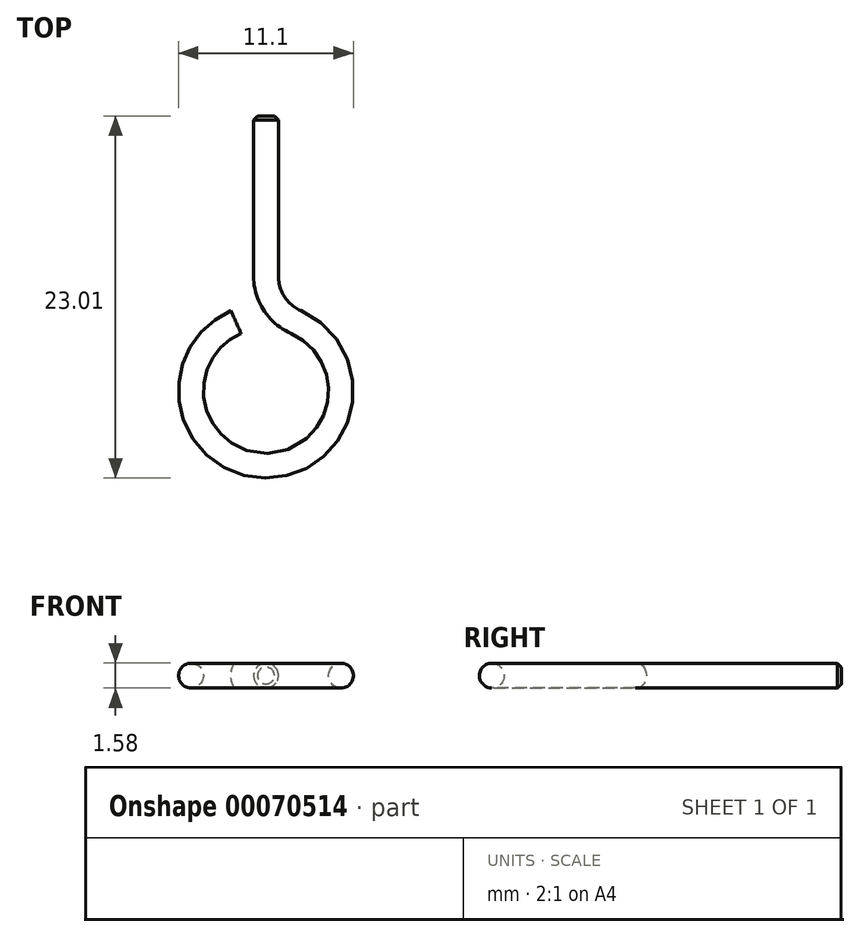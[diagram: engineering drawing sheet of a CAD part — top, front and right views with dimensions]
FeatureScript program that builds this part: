
annotation { "Feature Type Name" : "Feature", "Feature Type Description" : "" }
export const myFeature = defineFeature(function(context is Context, id is Id, definition is map)
    precondition{}
    {
        {
            var Q0;
            Q0=qCreatedBy(makeId("Top.planeOp"),FACE);
            var sketch = newSketch(context, id + "F0", { "sketchPlane" : qUnion([Q0])});
            skLineSegment(sketch, "E0", {"start": v(0, 17.46) * mm, "end": v(0, 7.27) * mm});
            skArc(sketch, "E1", {"start": v(1.9, 4.36) * mm, "mid": v(0, -4.76) * mm, "end": v(-1.9, 4.36) * mm});
            skPoint(sketch, "E2.visualSharp", {"position": v(0, 4.76) * mm});
            skArc(sketch, "E2.filletArc", {"start": v(0, 7.27) * mm, "mid": v(0.52, 5.54) * mm, "end": v(1.9, 4.36) * mm});
            skSolve(sketch);
        }
        {
            var Q0;
            Q0=qCreatedBy(makeId("Front.planeOp"),FACE);
            var Q1;
            Q1=sQuery(id+"F0.wireOp",VERTEX,"E0.start");
            cPlane(context, id + "F1", {"entities" : qUnion([Q0, Q1]), "cplaneType" : CPlaneType.PLANE_POINT, "offset" : 152.4 * mm, "width" : 152.4 * mm, "height" : 152.4 * mm});
        }
        {
            var Q0;
            Q0=qCreatedBy(id+"F1.planeOp",FACE);
            var sketch = newSketch(context, id + "F2", { "sketchPlane" : qUnion([Q0])});
            skCircle(sketch, "E3", {"center": v(0, 0) * mm, "radius": 0.79 * mm});
            skSolve(sketch);
        }
        {
            var Q0;
            Q0=makeQuery(id+"F2.imprint","IMPRINT",FACE,{"disambiguationData":[TD([[makeQuery(id+"F2.imprint","IMPRINT",EDGE,{"derivedFrom":sQuery(id+"F2.wireOp",EDGE,"E3")}),1.0]])]});
            var Q1;
            Q1=sQuery(id+"F0.wireOp",EDGE,"E0");
            var Q2;
            Q2=sQuery(id+"F0.wireOp",EDGE,"E2.filletArc");
            var Q3;
            Q3=sQuery(id+"F0.wireOp",EDGE,"E1");
            sweep(context, id + "F3", {"profiles" : qUnion([Q0]), "path" : qUnion([Q1, Q2, Q3])});
        }
        {
            var Q0;
            Q0=makeQuery(id+"F3.opSweep","CAP_EDGE",EDGE,{"disambiguationData":[OSD([sQuery(id+"F0.wireOp",VERTEX,"E0.start"),sQuery(id+"F2.wireOp",EDGE,"E3")])],"isStart":true});
            chamfer(context, id + "F4", {"entities" : qUnion([Q0]), "width" : 0.25 * mm, "tangentPropagation" : true});
        }
    });
